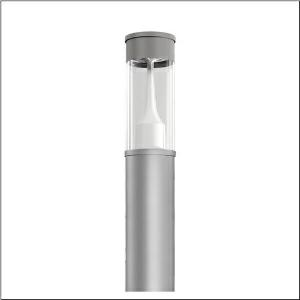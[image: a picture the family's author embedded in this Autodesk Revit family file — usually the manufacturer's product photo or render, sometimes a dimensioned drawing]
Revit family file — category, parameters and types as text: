
# Revit family: city-light_400_iq___st1_2a_5xa5305ef14hp_9457
name_source: partatom
category: Lighting Fixtures
units: mm (PartAtom-declared; Revit-internal decimal feet)

## family parameters
Cut with Voids When Loaded = No
Host = Face
Light Source = No
Part Type = Normal
Room Calculation Point = No
Round Connector Dimension = Use Diameter
Shared = No

## types (1)
- --- (1 x LED, 4730 lm, 33.6 W, 3000K)
    Apparent Load = 34 VA
    CIE Flux Codes = 22 61 94 96 100
    Color Rendering = 70
    Color Temperature = 3000K
    Default Elevation = 1800 mm
    Description = City-Light 400 iQ, light pillar, Module 540 iQ-SR, primary light control with 3 zone facetted reflector, of plastic, silver coated, highly specular, structured, primary optical cover: cover, of PMMA, transparent, partly coated, light distribution: ST1.2a, primary light characteristic: asymmetric, LED, High Power LED, rated luminous flux: 4.730lm, luminous efficacy: 141lm/W, light colour: 730, colour temperature: 3000K, control gear: iQ Street-Remote, control: pre-setting: logarithmic dimming characteristic, Street-Remote, Auto-Match, Temp-Guard, Lumen-Switch, Night-Set, Smart-Wire, Light-Fading, Desk-Remote (wireless, voltage-free reading and setting of iQ features in the workshop via application-optimized NFC function/RFID function), optimised constant luminous flux control (CLO 2.0), with terminal, 6-pole, max. 2.5mm², mains connection: 230..240V, AC, 50/60Hz, start of lifetime: 34W, end of service life: 36W, reduction: 15W, luminaire housing, cylindrical, of extruded aluminium section, coated, Siteco® metallic grey (DB 702S), length: 4.694mm, diameter: 200mm, Module 540 iQ-SR, traffic white (RAL 9016), equipment: Power, protection rating (complete): IP65, insulation class (complete): insulation class II (safety insulation), certification: CE, ENEC, VDE, packaging unit: 1 piece

Light Distribution: ST1.2a
    Height = 500 mm
    Lamp = 1 x LED
    Lamp Light Flux = 4730 lm
    Lamp Power = 33.6 W
    Lamp count = 1
    Length = 200 mm
    Luminous efficacy = 141 lm/W
    Manufacturer = Siteco
    ModVariant = No
    Model = 5XA5305EF14HP
    Mounting Place = Floor
    Mounting Type = Freestanding
    Number of Poles = 1
    OnlyDefault = Yes
    Power Factor = 1
    Product Name = City-Light 400 iQ | ST1.2a
    Product group = light pillar
    ProductGroupID = 1301
    Protection Class = Protection class II
    Protection Degree = IP 65
    RLX_Detail_Level = 1
    RLX_Emergency_Light_Flux = 0 lm
    RLX_Emergency_Type = 0
    RLX_Emergency_Type_DB = No
    RlxData = <blob elided: 53409 chars, md5=aa5b63cf>
    Socket = socket
    Standby Power = 0 W
    System Light Flux = 4730 lm
    System Power = 34 W
    Type Comments = factory setting: luminous flux: 100 % | dim-lin: 254 | 695 mA
    Type Image = l_1006916.jpg
    URL = http://relux.com
    VarID = @adj_191881
    Voltage = 0 V
    Weight = 0.00 kg
    Width = 0 mm  [stored 0 ft]

note: [stored X ft] marks values corroborated as IEEE doubles in the binary element streams (Revit-internal decimal feet)

## geometry (parser evidence)
native form markers: Blend x4, Sweep x9
no freeform markers — native parametric forms only
